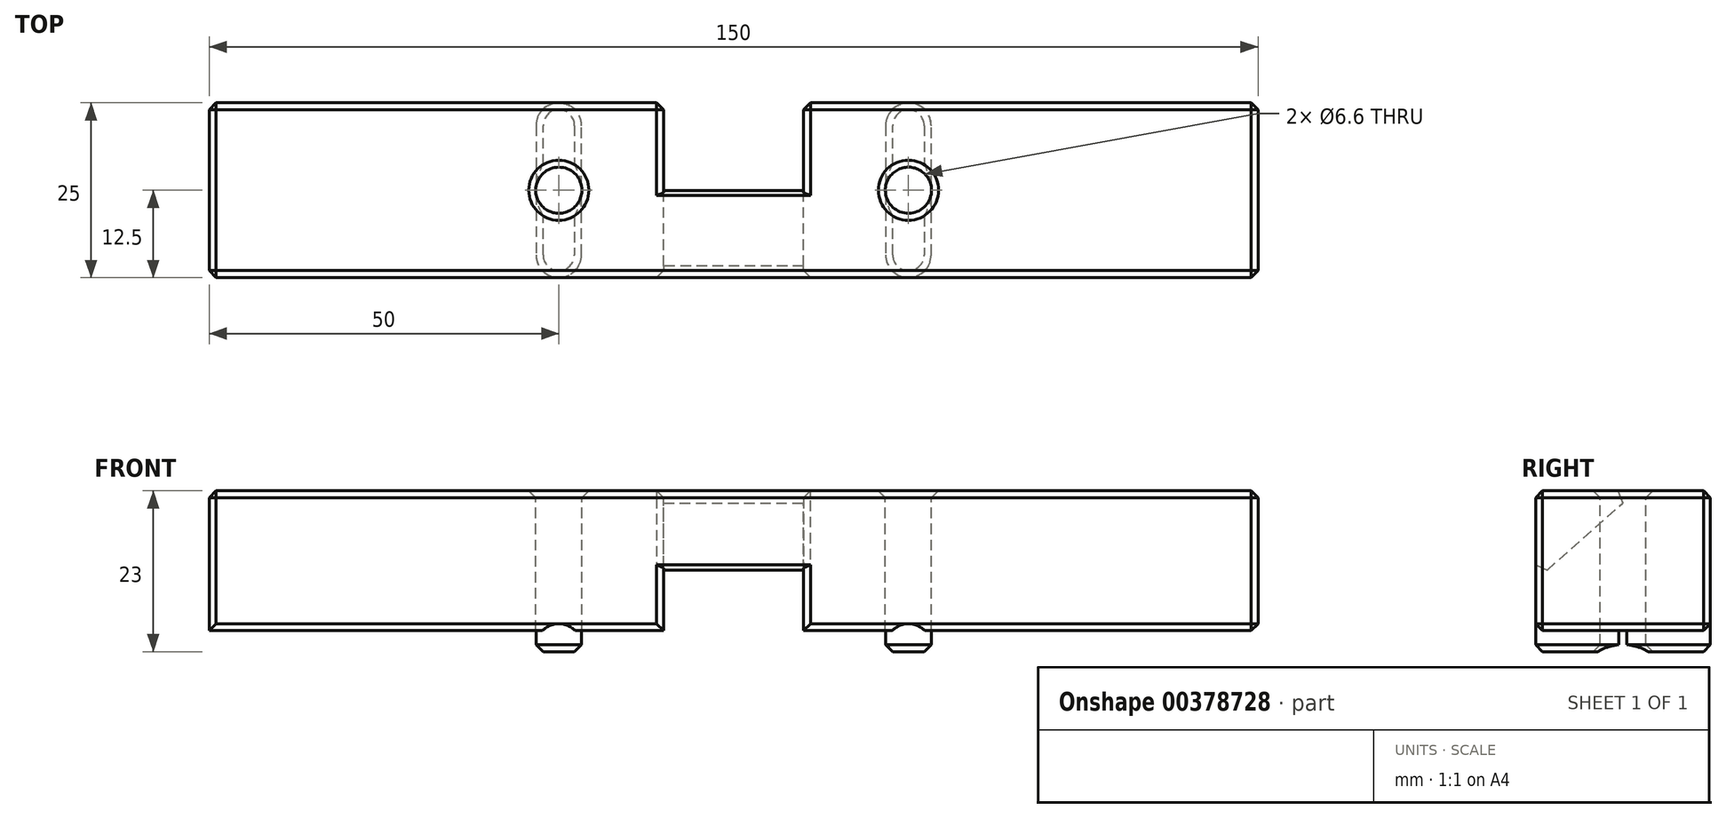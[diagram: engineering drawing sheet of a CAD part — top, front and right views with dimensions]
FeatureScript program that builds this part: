
annotation { "Feature Type Name" : "Feature", "Feature Type Description" : "" }
export const myFeature = defineFeature(function(context is Context, id is Id, definition is map)
    precondition{}
    {
        {
            var Q0;
            Q0=qCreatedBy(makeId("Front.planeOp"),FACE);
            var sketch = newSketch(context, id + "F0", { "sketchPlane" : qUnion([Q0]), "disableImprinting" : false});
            skLineSegment(sketch, "E0", {"start": v(0, 0) * mm, "end": v(-21.75, 0) * mm});
            skLineSegment(sketch, "E1", {"start": v(-21.75, 0) * mm, "end": v(-21.75, -3) * mm});
            skLineSegment(sketch, "E2", {"start": v(-21.75, -3) * mm, "end": v(-28.25, -3) * mm});
            skLineSegment(sketch, "E3", {"start": v(-28.25, -3) * mm, "end": v(-28.25, 0) * mm});
            skLineSegment(sketch, "E4", {"start": v(-28.25, 0) * mm, "end": v(-75, 0) * mm});
            skLineSegment(sketch, "E5", {"start": v(-75, 0) * mm, "end": v(-75, 20) * mm});
            skLineSegment(sketch, "E6", {"start": v(-75, 20) * mm, "end": v(0, 20) * mm});
            skLineSegment(sketch, "E7.MirrorCS", {"start": v(75, 20) * mm, "end": v(0, 20) * mm});
            skLineSegment(sketch, "E8.MirrorCS", {"start": v(75, 0) * mm, "end": v(75, 20) * mm});
            skLineSegment(sketch, "E9.MirrorCS", {"start": v(28.25, 0) * mm, "end": v(75, 0) * mm});
            skLineSegment(sketch, "E10.MirrorCS", {"start": v(28.25, -3) * mm, "end": v(28.25, 0) * mm});
            skLineSegment(sketch, "E11.MirrorCS", {"start": v(21.75, -3) * mm, "end": v(28.25, -3) * mm});
            skLineSegment(sketch, "E12.MirrorCS", {"start": v(21.75, 0) * mm, "end": v(21.75, -3) * mm});
            skLineSegment(sketch, "E13.MirrorCS", {"start": v(0, 0) * mm, "end": v(21.75, 0) * mm});
            skPoint(sketch, "E14", {"position": v(-25, -3) * mm});
            skPoint(sketch, "E15.MirrorP", {"position": v(25, -3) * mm});
            skSolve(sketch);
        }
        {
            var Q0;
            Q0 = qSketchRegion(id + "F0", true);
            extrude(context, id + "F1", {"entities" : qUnion([Q0]), "depth" : 25 * mm, "symmetric" : true});
        }
        {
            var Q0;
            Q0=makeQuery(id+"F1.opExtrude","SWEPT_FACE",FACE,{"disambiguationData":[OSD([sQuery(id+"F0.wireOp",EDGE,"E2")])]});
            var sketch = newSketch(context, id + "F2", { "sketchPlane" : qUnion([Q0])});
            skPoint(sketch, "E16", {"position": v(-25, 0) * mm});
            skLineSegment(sketch, "E17", {"start": v(-28.25, 0) * mm, "end": v(-21.75, 0) * mm, "construction": true});
            skPoint(sketch, "E18.MirrorP", {"position": v(25, 0) * mm});
            skSolve(sketch);
        }
        {
            var Q0;
            Q0=sQuery(id+"F2.wireOp",VERTEX,"E16");
            var Q1;
            Q1=sQuery(id+"F2.wireOp",VERTEX,"E18.MirrorP");
            var Q2;
            Q2=makeQuery(id+"F1.opExtrude","SWEPT_BODY",BODY,{"disambiguationData":[OSD([sQuery(id+"F0.wireOp",EDGE,"E0"),sQuery(id+"F0.wireOp",EDGE,"E1"),sQuery(id+"F0.wireOp",EDGE,"E2"),sQuery(id+"F0.wireOp",EDGE,"E3"),sQuery(id+"F0.wireOp",EDGE,"E4"),sQuery(id+"F0.wireOp",EDGE,"E5"),sQuery(id+"F0.wireOp",EDGE,"E6"),sQuery(id+"F0.wireOp",EDGE,"E7.MirrorCS"),sQuery(id+"F0.wireOp",EDGE,"E8.MirrorCS"),sQuery(id+"F0.wireOp",EDGE,"E9.MirrorCS"),sQuery(id+"F0.wireOp",EDGE,"E10.MirrorCS"),sQuery(id+"F0.wireOp",EDGE,"E11.MirrorCS"),sQuery(id+"F0.wireOp",EDGE,"E12.MirrorCS"),sQuery(id+"F0.wireOp",EDGE,"E13.MirrorCS")])]});
            hole(context, id + "F3", {"style" : HoleStyle.SIMPLE, "endStyle" : HoleEndStyle.THROUGH, "standardTappedOrClearance" : lookupTablePath({ "standard" : "ISO", "fit" : "Normal", "size" : "M6", "type" : "Clearance" }), "standardBlindInLast" : lookupTablePath({ "fit" : "Standard", "standard" : "ISO", "size" : "M6", "type" : "Clearance" }), "holeDiameter" : 6.6 * mm, "isTappedThrough" : true, "tappedDepth" : 12 * mm, "tapClearance" : 3, "locations" : qUnion([Q0, Q1]), "scope" : qUnion([Q2]), "startStyle" : HoleStartStyle.PART});
        }
        {
            var Q0;
            Q0=qCreatedBy(makeId("Right.planeOp"),FACE);
            var sketch = newSketch(context, id + "F4", { "sketchPlane" : qUnion([Q0])});
            skLineSegment(sketch, "E19", {"start": v(-12.5, 0) * mm, "end": v(-12.5, 7.17) * mm});
            skLineSegment(sketch, "E20", {"start": v(-12.5, 7.17) * mm, "end": v(1.91, 20) * mm});
            skLineSegment(sketch, "E21", {"start": v(1.91, 20) * mm, "end": v(12.5, 20) * mm});
            skLineSegment(sketch, "E22", {"start": v(12.5, 20) * mm, "end": v(12.5, 0) * mm});
            skLineSegment(sketch, "E23", {"start": v(12.5, 0) * mm, "end": v(-12.5, 0) * mm});
            skSolve(sketch);
        }
        {
            var Q0;
            Q0 = qSketchRegion(id + "F4", true);
            extrude(context, id + "F5", {"entities" : qUnion([Q0]), "operationType" : NewBodyOperationType.REMOVE, "depth" : 20 * mm, "symmetric" : true});
        }
        {
            var Q0;
            Q0=makeQuery(id+"F1.opExtrude","CAP_EDGE",EDGE,{"disambiguationData":[OSD([sQuery(id+"F0.wireOp",EDGE,"E3")])],"isStart":false});
            var Q1;
            Q1=makeQuery(id+"F1.opExtrude","CAP_EDGE",EDGE,{"disambiguationData":[OSD([sQuery(id+"F0.wireOp",EDGE,"E1")])],"isStart":false});
            var Q2;
            Q2=makeQuery(id+"F1.opExtrude","CAP_EDGE",EDGE,{"disambiguationData":[OSD([sQuery(id+"F0.wireOp",EDGE,"E12.MirrorCS")])],"isStart":false});
            var Q3;
            Q3=makeQuery(id+"F1.opExtrude","CAP_EDGE",EDGE,{"disambiguationData":[OSD([sQuery(id+"F0.wireOp",EDGE,"E10.MirrorCS")])],"isStart":false});
            var Q4;
            Q4=makeQuery(id+"F1.opExtrude","CAP_EDGE",EDGE,{"disambiguationData":[OSD([sQuery(id+"F0.wireOp",EDGE,"E10.MirrorCS")])],"isStart":true});
            var Q5;
            Q5=makeQuery(id+"F1.opExtrude","CAP_EDGE",EDGE,{"disambiguationData":[OSD([sQuery(id+"F0.wireOp",EDGE,"E12.MirrorCS")])],"isStart":true});
            var Q6;
            Q6=makeQuery(id+"F1.opExtrude","CAP_EDGE",EDGE,{"disambiguationData":[OSD([sQuery(id+"F0.wireOp",EDGE,"E1")])],"isStart":true});
            var Q7;
            Q7=makeQuery(id+"F1.opExtrude","CAP_EDGE",EDGE,{"disambiguationData":[OSD([sQuery(id+"F0.wireOp",EDGE,"E3")])],"isStart":true});
            fillet(context, id + "F6", {"entities" : qUnion([Q0, Q1, Q2, Q3, Q4, Q5, Q6, Q7]), "radius" : 3.25 * mm, "tangentPropagation" : true, "allowEdgeOverflow" : false});
        }
        {
            var Q0;
            Q0=makeQuery(id+"F1.opExtrude","SWEPT_FACE",FACE,{"disambiguationData":[OSD([sQuery(id+"F0.wireOp",EDGE,"E6"),sQuery(id+"F0.wireOp",EDGE,"E7.MirrorCS")])]});
            var Q1;
            Q1=makeQuery(id+"F1.opExtrude","CAP_FACE",FACE,{"disambiguationData":[OSD([sQuery(id+"F0.wireOp",EDGE,"E0"),sQuery(id+"F0.wireOp",EDGE,"E1"),sQuery(id+"F0.wireOp",EDGE,"E2"),sQuery(id+"F0.wireOp",EDGE,"E3"),sQuery(id+"F0.wireOp",EDGE,"E4"),sQuery(id+"F0.wireOp",EDGE,"E5"),sQuery(id+"F0.wireOp",EDGE,"E6"),sQuery(id+"F0.wireOp",EDGE,"E7.MirrorCS"),sQuery(id+"F0.wireOp",EDGE,"E8.MirrorCS"),sQuery(id+"F0.wireOp",EDGE,"E9.MirrorCS"),sQuery(id+"F0.wireOp",EDGE,"E10.MirrorCS"),sQuery(id+"F0.wireOp",EDGE,"E11.MirrorCS"),sQuery(id+"F0.wireOp",EDGE,"E12.MirrorCS"),sQuery(id+"F0.wireOp",EDGE,"E13.MirrorCS")])],"isStart":false});
            var Q2;
            Q2=makeQuery(id+"F1.opExtrude","SWEPT_FACE",FACE,{"disambiguationData":[OSD([sQuery(id+"F0.wireOp",EDGE,"E8.MirrorCS")])]});
            var Q3;
            {var subQ0=sQuery(id+"F0.wireOp",EDGE,"E9.MirrorCS");var subQ1=sQuery(id+"F0.wireOp",EDGE,"E8.MirrorCS");var subQ2=sQuery(id+"F0.wireOp",EDGE,"E7.MirrorCS");var subQ3=sQuery(id+"F0.wireOp",EDGE,"E6");var subQ4=sQuery(id+"F0.wireOp",EDGE,"E13.MirrorCS");var subQ5=sQuery(id+"F0.wireOp",EDGE,"E0");var subQ6=sQuery(id+"F0.wireOp",EDGE,"E12.MirrorCS");var subQ7=sQuery(id+"F0.wireOp",EDGE,"E10.MirrorCS");var subQ8=sQuery(id+"F0.wireOp",EDGE,"E11.MirrorCS");Q3=makeQuery(id+"F5.boolean.opBoolean","SPLIT",FACE,{"disambiguationData":[TD([makeQuery(id+"F1.opExtrude","SWEPT_FACE",FACE,{"disambiguationData":[OSD([subQ1])]})])],"derivedFrom":makeQuery(id+"F1.opExtrude","CAP_FACE",FACE,{"disambiguationData":[OSD([subQ5,sQuery(id+"F0.wireOp",EDGE,"E1"),sQuery(id+"F0.wireOp",EDGE,"E2"),sQuery(id+"F0.wireOp",EDGE,"E3"),sQuery(id+"F0.wireOp",EDGE,"E4"),sQuery(id+"F0.wireOp",EDGE,"E5"),subQ3,subQ2,subQ1,subQ0,subQ7,subQ8,subQ6,subQ4])],"isStart":true})});}
            var Q4;
            {var subQ0=sQuery(id+"F0.wireOp",EDGE,"E3");var subQ1=sQuery(id+"F0.wireOp",EDGE,"E2");var subQ2=sQuery(id+"F0.wireOp",EDGE,"E1");var subQ3=sQuery(id+"F0.wireOp",EDGE,"E13.MirrorCS");var subQ4=sQuery(id+"F0.wireOp",EDGE,"E0");var subQ5=sQuery(id+"F0.wireOp",EDGE,"E4");var subQ6=sQuery(id+"F0.wireOp",EDGE,"E5");var subQ7=sQuery(id+"F0.wireOp",EDGE,"E7.MirrorCS");var subQ8=sQuery(id+"F0.wireOp",EDGE,"E6");Q4=makeQuery(id+"F5.boolean.opBoolean","SPLIT",FACE,{"disambiguationData":[TD([makeQuery(id+"F1.opExtrude","SWEPT_FACE",FACE,{"disambiguationData":[OSD([subQ2])]})])],"derivedFrom":makeQuery(id+"F1.opExtrude","CAP_FACE",FACE,{"disambiguationData":[OSD([subQ4,subQ2,subQ1,subQ0,subQ5,subQ6,subQ8,subQ7,sQuery(id+"F0.wireOp",EDGE,"E8.MirrorCS"),sQuery(id+"F0.wireOp",EDGE,"E9.MirrorCS"),sQuery(id+"F0.wireOp",EDGE,"E10.MirrorCS"),sQuery(id+"F0.wireOp",EDGE,"E11.MirrorCS"),sQuery(id+"F0.wireOp",EDGE,"E12.MirrorCS"),subQ3])],"isStart":true})});}
            var Q5;
            Q5=makeQuery(id+"F1.opExtrude","SWEPT_FACE",FACE,{"disambiguationData":[OSD([sQuery(id+"F0.wireOp",EDGE,"E11.MirrorCS")])]});
            var Q6;
            Q6=makeQuery(id+"F1.opExtrude","SWEPT_FACE",FACE,{"disambiguationData":[OSD([sQuery(id+"F0.wireOp",EDGE,"E2")])]});
            chamfer(context, id + "F7", {"entities" : qUnion([Q0, Q1, Q2, Q3, Q4, Q5, Q6]), "width" : 1 * mm, "tangentPropagation" : true});
        }
    });
